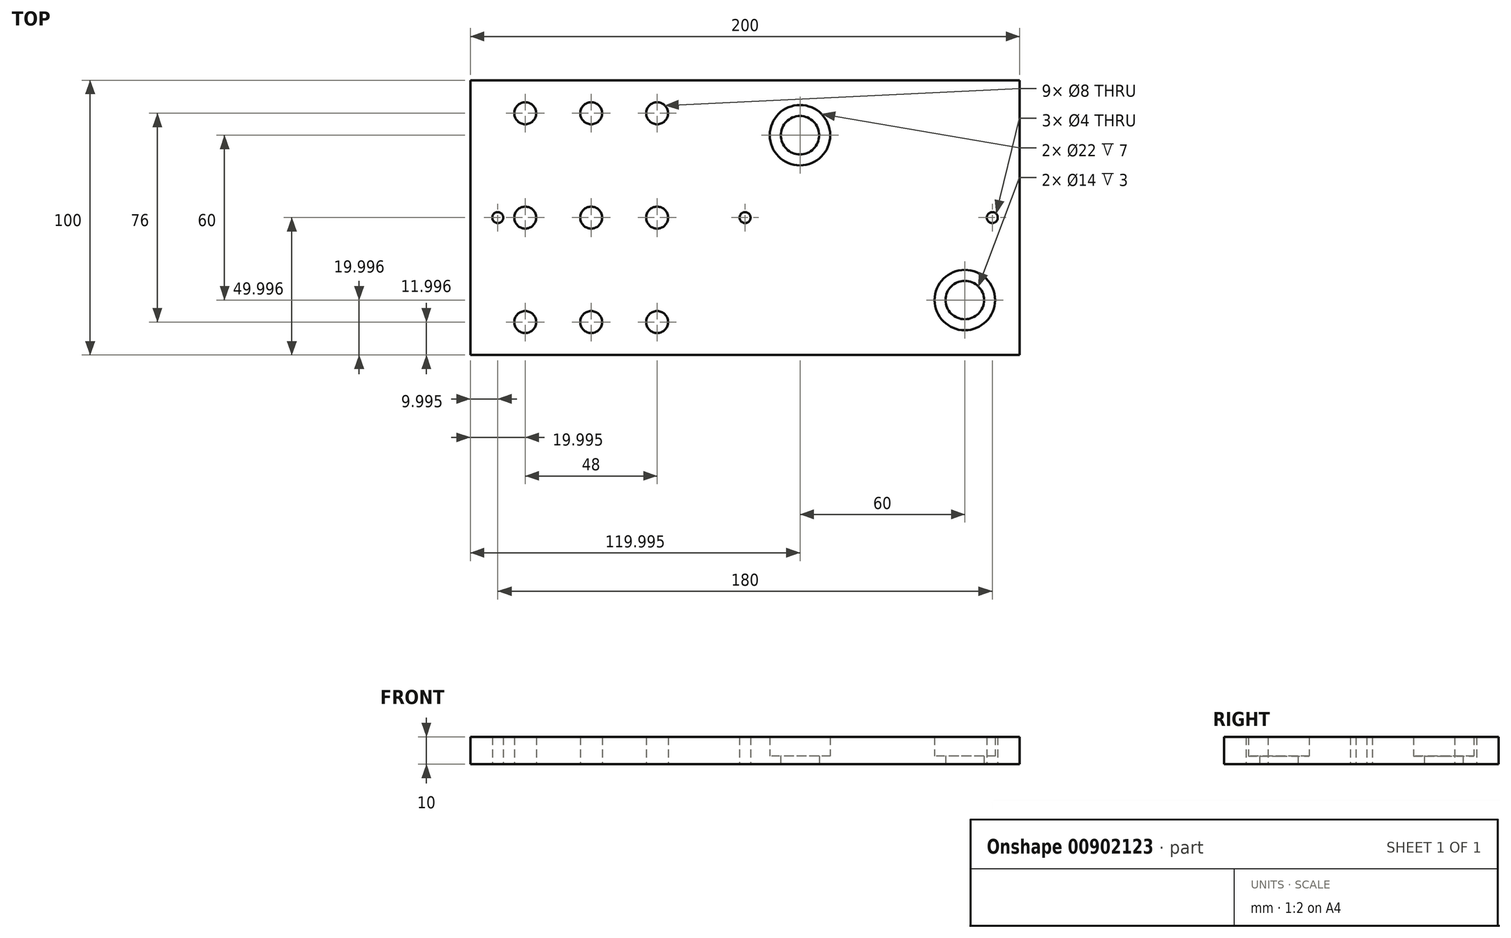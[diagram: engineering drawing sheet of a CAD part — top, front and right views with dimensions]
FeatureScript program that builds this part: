
annotation { "Feature Type Name" : "Feature", "Feature Type Description" : "" }
export const myFeature = defineFeature(function(context is Context, id is Id, definition is map)
    precondition{}
    {
        {
            var Q0;
            Q0=qCreatedBy(makeId("Top.planeOp"),FACE);
            var sketch = newSketch(context, id + "F0", { "sketchPlane" : qUnion([Q0])});
            skLineSegment(sketch, "E0.bottom", {"start": v(-136.01, 62.84) * mm, "end": v(63.99, 62.84) * mm});
            skLineSegment(sketch, "E0.top", {"start": v(-136.01, -37.16) * mm, "end": v(63.99, -37.16) * mm});
            skLineSegment(sketch, "E0.left", {"start": v(-136.01, 62.84) * mm, "end": v(-136.01, -37.16) * mm});
            skLineSegment(sketch, "E0.right", {"start": v(63.99, 62.84) * mm, "end": v(63.99, -37.16) * mm});
            skCircle(sketch, "E1", {"center": v(-116.01, 50.84) * mm, "radius": 4 * mm});
            skCircle(sketch, "E2.MirrorC", {"center": v(-116.01, -25.16) * mm, "radius": 4 * mm});
            skCircle(sketch, "E3.MirrorC", {"center": v(-68.01, 50.84) * mm, "radius": 4 * mm});
            skCircle(sketch, "E4.MirrorC", {"center": v(-68.01, -25.16) * mm, "radius": 4 * mm});
            skCircle(sketch, "E5", {"center": v(-126.01, 12.84) * mm, "radius": 2 * mm});
            skCircle(sketch, "E6", {"center": v(-36.01, 12.84) * mm, "radius": 2 * mm});
            skCircle(sketch, "E7", {"center": v(53.99, 12.84) * mm, "radius": 2 * mm});
            skLineSegment(sketch, "E8", {"start": v(63.99, -37.16) * mm, "end": v(43.99, -37.16) * mm});
            skLineSegment(sketch, "E9", {"start": v(43.99, -37.16) * mm, "end": v(43.99, -17.16) * mm});
            skCircle(sketch, "E10", {"center": v(-16.01, 42.84) * mm, "radius": 7 * mm});
            skCircle(sketch, "E11", {"center": v(-16.01, 42.84) * mm, "radius": 11 * mm});
            skCircle(sketch, "E12", {"center": v(43.99, -17.16) * mm, "radius": 7 * mm});
            skCircle(sketch, "E13", {"center": v(43.99, -17.16) * mm, "radius": 11 * mm});
            skCircle(sketch, "E14", {"center": v(-92.01, 50.84) * mm, "radius": 4 * mm});
            skCircle(sketch, "E15", {"center": v(-116.01, 12.84) * mm, "radius": 4 * mm});
            skCircle(sketch, "E16", {"center": v(-92.01, 12.84) * mm, "radius": 4 * mm});
            skCircle(sketch, "E17", {"center": v(-68.01, 12.84) * mm, "radius": 4 * mm});
            skCircle(sketch, "E18", {"center": v(-92.01, -25.16) * mm, "radius": 4 * mm});
            skSolve(sketch);
        }
        {
            var Q0;
            Q0=makeQuery(id+"F0.imprint","IMPRINT",FACE,{"disambiguationData":[TD([[makeQuery(id+"F0.imprint","IMPRINT",EDGE,{"derivedFrom":sQuery(id+"F0.wireOp",EDGE,"E0.bottom")}),-1.0]])]});
            extrude(context, id + "F1", {"entities" : qUnion([Q0]), "depth" : 10 * mm, "offsetDistance" : 25 * mm});
        }
        {
            var Q0;
            Q0=makeQuery(id+"F0.imprint","IMPRINT",FACE,{"disambiguationData":[TD([[makeQuery(id+"F0.imprint","IMPRINT",EDGE,{"derivedFrom":sQuery(id+"F0.wireOp",EDGE,"E10")}),-1.0]])]});
            var Q1;
            Q1=makeQuery(id+"F0.imprint","IMPRINT",FACE,{"disambiguationData":[TD([[makeQuery(id+"F0.imprint","IMPRINT",EDGE,{"derivedFrom":sQuery(id+"F0.wireOp",EDGE,"E12")}),-1.0]])]});
            extrude(context, id + "F2", {"entities" : qUnion([Q0, Q1]), "operationType" : NewBodyOperationType.ADD, "depth" : 3 * mm, "offsetDistance" : 25 * mm});
        }
    });
